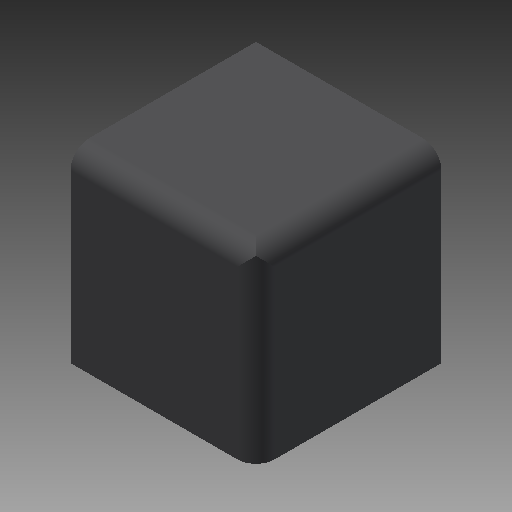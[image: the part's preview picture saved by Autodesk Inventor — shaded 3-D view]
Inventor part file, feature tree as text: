
AUTODESK INVENTOR PART (.ipt)
format: ipt  version: 2018 (Build 220112000, 112)  size: 330,240 bytes
history: native  units: mm
features: sketch x31, extrude x30, other x21, revolve x1
ambient origin geometry x8: Origin, YZ Plane, XZ Plane, XY Plane, X Axis, Y Axis, Z Axis, Center Point
bodies: Solid1 (feature_tree)
feature tree (83):
  extrude  "Extrusion1"  Depth=5.0mm TaperAngle=0.0deg
  sketch  "Sketch_2"  dims[d4=5.0mm d5=0.0mm d6=4.0mm d7=-0.872665mm]
  extrude  "Extrusion2"  Depth=4.0mm
  extrude  "Extrusion3"  Depth=4.0mm
  extrude  "Extrusion4"  Depth=4.0mm
  extrude  "Extrusion5"  Depth=8.5mm TaperAngle=0.0deg
  extrude  "Extrusion6"  Depth=4.0mm
  extrude  "Extrusion7"  Depth=4.0mm
  extrude  "Extrusion8"  Depth=4.0mm
  extrude  "Extrusion9"  Depth=4.0mm
  extrude  "Extrusion10"  Depth=4.0mm
  extrude  "Extrusion11"  TaperAngle=360.0deg  [1 undecoded]
  sketch  "Sketch_12"  dims[d43=40.0mm d44=0.0mm d45=40.0mm d46=0.0mm]
  sketch  "Sketch_13"  dims[d47=40.0mm d48=0.0mm d49=40.0mm d50=0.0mm]
  extrude  "Extrusion12"  Depth=40.0mm TaperAngle=0.0deg
  extrude  "Extrusion13"  Depth=40.0mm TaperAngle=0.0deg
  extrude  "Extrusion14"  Depth=36.0mm TaperAngle=0.0deg
  extrude  "Extrusion15"  Depth=4.0mm
  extrude  "Extrusion16"  [1 undecoded]
  extrude  "Extrusion17"  [1 undecoded]
  extrude  "Extrusion18"  [1 undecoded]
  extrude  "Extrusion19"  [1 undecoded]
  extrude  "Extrusion20"  [1 undecoded]
  extrude  "Extrusion21"  [1 undecoded]
  sketch  "Sketch_24"
  revolve  "Revolution1"  [1 undecoded]
  extrude  "Extrusion22"  [1 undecoded]
  extrude  "Extrusion23"  [1 undecoded]
  extrude  "Extrusion24"  [1 undecoded]
  extrude  "Extrusion25"  [1 undecoded]
  extrude  "Extrusion26"  [1 undecoded]
  sketch  "Sketch_30"
  extrude  "Extrusion27"  [1 undecoded]
  extrude  "Extrusion28"  [1 undecoded]
  extrude  "Extrusion29"  [1 undecoded]
  extrude  "Extrusion30"  [1 undecoded]
  other  "side_1_XY"
  other  "side_1_YZ"
  other  "side_1_ZX"
  other  "side_1_X"
  other  "side_1_Y"
  other  "side_1_Z"
  other  "side_1_Center"
  other  "side_2_XY"
  other  "side_2_YZ"
  other  "side_2_ZX"
  other  "side_2_X"
  other  "side_2_Y"
  other  "side_2_Z"
  other  "side_2_Center"
  other  "side_3_XY"
  other  "side_3_YZ"
  other  "side_3_ZX"
  other  "side_3_X"
  other  "side_3_Y"
  other  "side_3_Z"
  other  "side_3_Center"
  sketch  "Sketch_1"  dims[d0=5.0mm d1=0.0mm d2=5.0mm d3=0.0mm]
  sketch  "Sketch_3"  dims[d8=4.0mm d9=-0.872665mm d10=4.0mm d11=-0.872665mm]
  sketch  "Sketch_4"  dims[d12=4.0mm d13=-0.872665mm d14=4.0mm d15=-0.872665mm]
  sketch  "Sketch_5"  dims[d16=4.0mm d17=-0.872665mm d18=8.5mm d19=0.0mm]
  sketch  "Sketch_6"  dims[d20=6.0mm d21=0.0mm d22=4.0mm d23=-0.872665mm]
  sketch  "Sketch_7"  dims[d24=4.0mm d25=-0.872665mm d26=4.0mm d27=-0.872665mm]
  sketch  "Sketch_8"  dims[d28=4.0mm d29=-0.872665mm d30=4.0mm d31=-0.872665mm]
  sketch  "Sketch_9"  dims[d32=4.0mm d33=-0.872665mm d34=4.0mm d35=-0.872665mm]
  sketch  "Sketch_10"  dims[d36=4.0mm d37=-0.872665mm d38=4.0mm d39=-0.872665mm]
  sketch  "Sketch_11"  dims[d40=4.0mm d41=-0.872665mm d42=360.0deg]
  sketch  "Sketch_14"  dims[d51=40.0mm d52=0.0mm d53=36.0mm d54=0.0mm]
  sketch  "Sketch_15"  dims[d55=40.0mm d56=0.0mm d57=4.0mm d58=-0.872665mm]
  sketch  "Sketch_16"  dims[d59=4.0mm d60=-0.872665mm]
  sketch  "Sketch_17"
  sketch  "Sketch_18"
  sketch  "Sketch_19"
  sketch  "Sketch_20"
  sketch  "Sketch_21"
  sketch  "Sketch_22"
  sketch  "Sketch_23"
  sketch  "Sketch_26"
  sketch  "Sketch_28"
  sketch  "Sketch_29"
  sketch  "Sketch_25"
  sketch  "Sketch_27"
  sketch  "Sketch_31"
note: 17 required parameter values undecoded (feature->parameter linkage not recoverable at this tier; creation-order binding heuristic only, values carry confidence <= 0.55)
